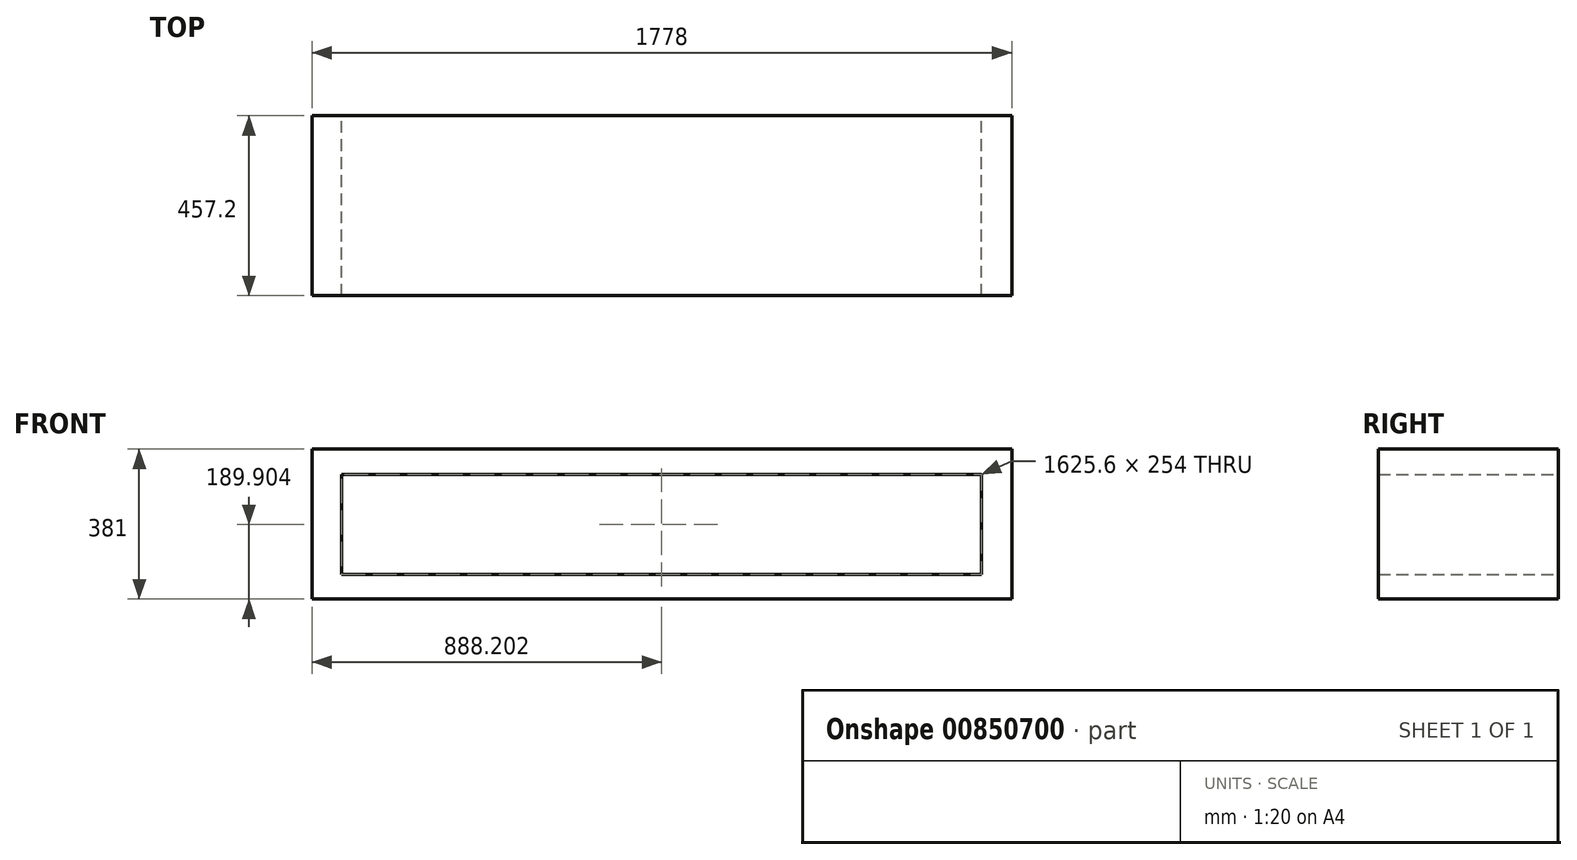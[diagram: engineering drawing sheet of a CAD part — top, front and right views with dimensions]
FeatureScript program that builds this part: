
annotation { "Feature Type Name" : "Feature", "Feature Type Description" : "" }
export const myFeature = defineFeature(function(context is Context, id is Id, definition is map)
    precondition{}
    {
        {
            var Q0;
            Q0=qCreatedBy(makeId("Front.planeOp"),FACE);
            var sketch = newSketch(context, id + "F0", { "sketchPlane" : qUnion([Q0])});
            skLineSegment(sketch, "E0.bottom", {"start": v(-899.92, -259.8) * mm, "end": v(878.08, -259.8) * mm});
            skLineSegment(sketch, "E0.top", {"start": v(-899.92, -640.8) * mm, "end": v(878.08, -640.8) * mm});
            skLineSegment(sketch, "E0.left", {"start": v(-899.92, -259.8) * mm, "end": v(-899.92, -640.8) * mm});
            skLineSegment(sketch, "E0.right", {"start": v(878.08, -259.8) * mm, "end": v(878.08, -640.8) * mm});
            skLineSegment(sketch, "E1.bottom", {"start": v(-824.52, -323.9) * mm, "end": v(801.08, -323.9) * mm});
            skLineSegment(sketch, "E1.top", {"start": v(-824.52, -577.9) * mm, "end": v(801.08, -577.9) * mm});
            skLineSegment(sketch, "E1.left", {"start": v(-824.52, -323.9) * mm, "end": v(-824.52, -577.9) * mm});
            skLineSegment(sketch, "E1.right", {"start": v(801.08, -323.9) * mm, "end": v(801.08, -577.9) * mm});
            skLineSegment(sketch, "E2", {"start": v(-899.92, -450.3) * mm, "end": v(-823.72, -450.3) * mm, "construction": true});
            skLineSegment(sketch, "E3", {"start": v(878.08, -450.3) * mm, "end": v(801.88, -450.3) * mm, "construction": true});
            skLineSegment(sketch, "E4", {"start": v(-10.92, -259.8) * mm, "end": v(-10.92, -323.3) * mm, "construction": true});
            skLineSegment(sketch, "E5", {"start": v(-10.92, -640.8) * mm, "end": v(-10.92, -577.3) * mm, "construction": true});
            skSolve(sketch);
        }
        {
            var Q0;
            Q0=makeQuery(id+"F0.imprint","IMPRINT",FACE,{"disambiguationData":[TD([[makeQuery(id+"F0.imprint","IMPRINT",EDGE,{"derivedFrom":sQuery(id+"F0.wireOp",EDGE,"E0.bottom")}),-1.0]])]});
            extrude(context, id + "F1", {"entities" : qUnion([Q0]), "depth" : 457.2 * mm, "offsetDistance" : 25.4 * mm});
        }
    });
